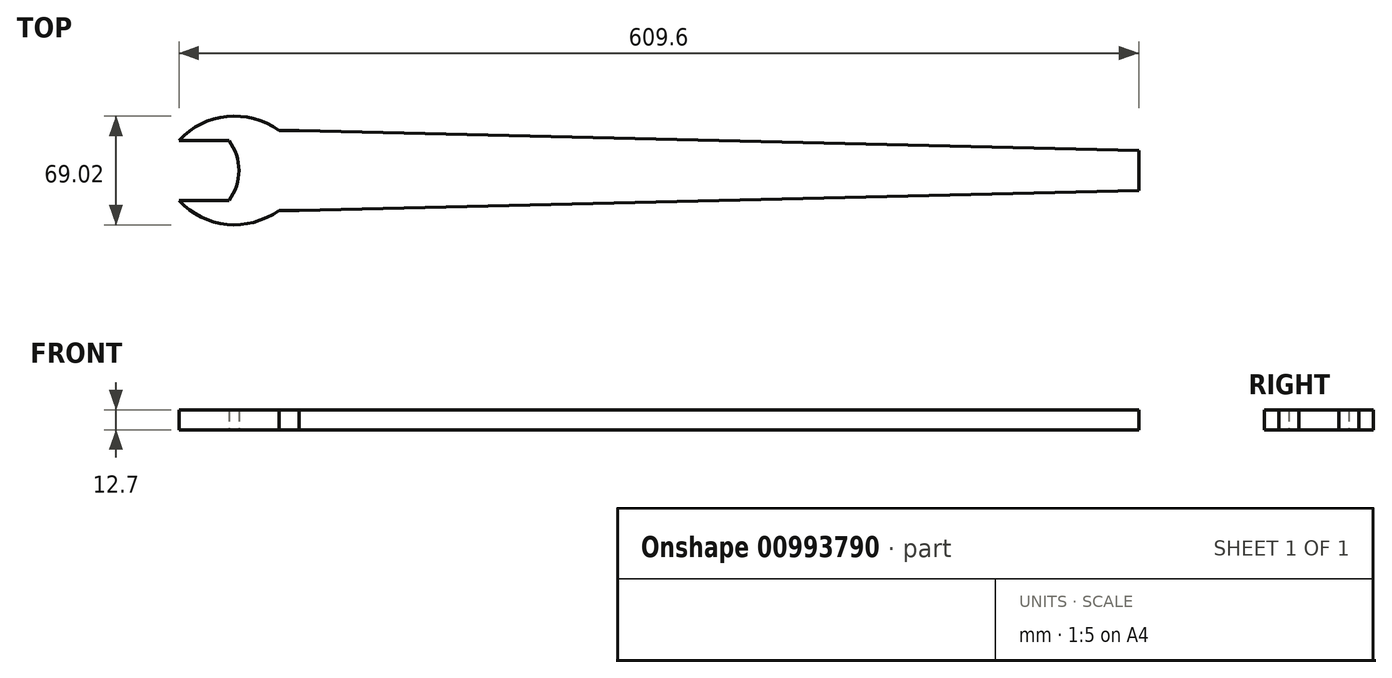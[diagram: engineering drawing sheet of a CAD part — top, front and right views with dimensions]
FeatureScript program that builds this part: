
annotation { "Feature Type Name" : "Feature", "Feature Type Description" : "" }
export const myFeature = defineFeature(function(context is Context, id is Id, definition is map)
    precondition{}
    {
        {
            var Q0;
            Q0=qCreatedBy(makeId("Top.planeOp"),FACE);
            var sketch = newSketch(context, id + "F0", { "sketchPlane" : qUnion([Q0])});
            skLineSegment(sketch, "E0", {"start": v(0, 0) * mm, "end": v(-609.6, 0) * mm});
            skLineSegment(sketch, "E1", {"start": v(-609.6, 0) * mm, "end": v(-609.6, 19.05) * mm, "construction": true});
            skLineSegment(sketch, "E2", {"start": v(-609.6, 0) * mm, "end": v(-609.6, -19.05) * mm, "construction": true});
            skLineSegment(sketch, "E3", {"start": v(-571.5, -19.07) * mm, "end": v(-571.5, 21.08) * mm, "construction": true});
            skLineSegment(sketch, "E4", {"start": v(-533.4, 0) * mm, "end": v(-533.4, -25.4) * mm, "construction": true});
            skLineSegment(sketch, "E5", {"start": v(-533.4, 0) * mm, "end": v(-533.4, 25.4) * mm, "construction": true});
            skLineSegment(sketch, "E6", {"start": v(0, 0) * mm, "end": v(0, -12.7) * mm});
            skLineSegment(sketch, "E7", {"start": v(0, 0) * mm, "end": v(0, 12.7) * mm});
            skLineSegment(sketch, "E8", {"start": v(-609.6, -19.05) * mm, "end": v(-562.08, -19.05) * mm});
            skLineSegment(sketch, "E9", {"start": v(-609.6, 19.05) * mm, "end": v(-557.46, 19.05) * mm});
            skLineSegment(sketch, "E10", {"start": v(-577.85, 19.05) * mm, "end": v(-577.85, -19.05) * mm});
            skArc(sketch, "E11", {"start": v(-577.85, -19.05) * mm, "mid": v(-571.48, 0) * mm, "end": v(-577.85, 19.05) * mm});
            skLineSegment(sketch, "E12", {"start": v(-584.2, 0) * mm, "end": v(-584.2, 30.15) * mm, "construction": true});
            skLineSegment(sketch, "E13", {"start": v(-533.4, -25.4) * mm, "end": v(-546.1, -25.4) * mm});
            skLineSegment(sketch, "E14.MirrorCS", {"start": v(-533.4, 25.4) * mm, "end": v(-546.1, 25.4) * mm});
            skArc(sketch, "E15", {"start": v(-609.6, -19.05) * mm, "mid": v(-579.05, -34.27) * mm, "end": v(-546.1, -25.4) * mm});
            skArc(sketch, "E16.MirrorCS", {"start": v(-609.6, 19.05) * mm, "mid": v(-579.05, 34.27) * mm, "end": v(-546.1, 25.4) * mm});
            skLineSegment(sketch, "E17", {"start": v(-533.4, -25.4) * mm, "end": v(0, -12.7) * mm});
            skLineSegment(sketch, "E18", {"start": v(-533.4, 25.4) * mm, "end": v(0, 12.7) * mm});
            skSolve(sketch);
        }
        {
            var Q0;
            {var subQ5=sQuery(id+"F0.wireOp",EDGE,"E7");Q0=makeQuery(id+"F0.imprint","IMPRINT",FACE,{"disambiguationData":[TD([[makeQuery(id+"F0.imprint","IMPRINT",EDGE,{"derivedFrom":subQ5}),1.0]])]});}
            var Q1;
            {var subQ6=sQuery(id+"F0.wireOp",EDGE,"E6");Q1=makeQuery(id+"F0.imprint","IMPRINT",FACE,{"disambiguationData":[TD([[makeQuery(id+"F0.imprint","IMPRINT",EDGE,{"derivedFrom":subQ6}),-1.0]])]});}
            extrude(context, id + "F1", {"entities" : qUnion([Q0, Q1]), "depth" : 12.7 * mm, "offsetDistance" : 25.4 * mm});
        }
    });
